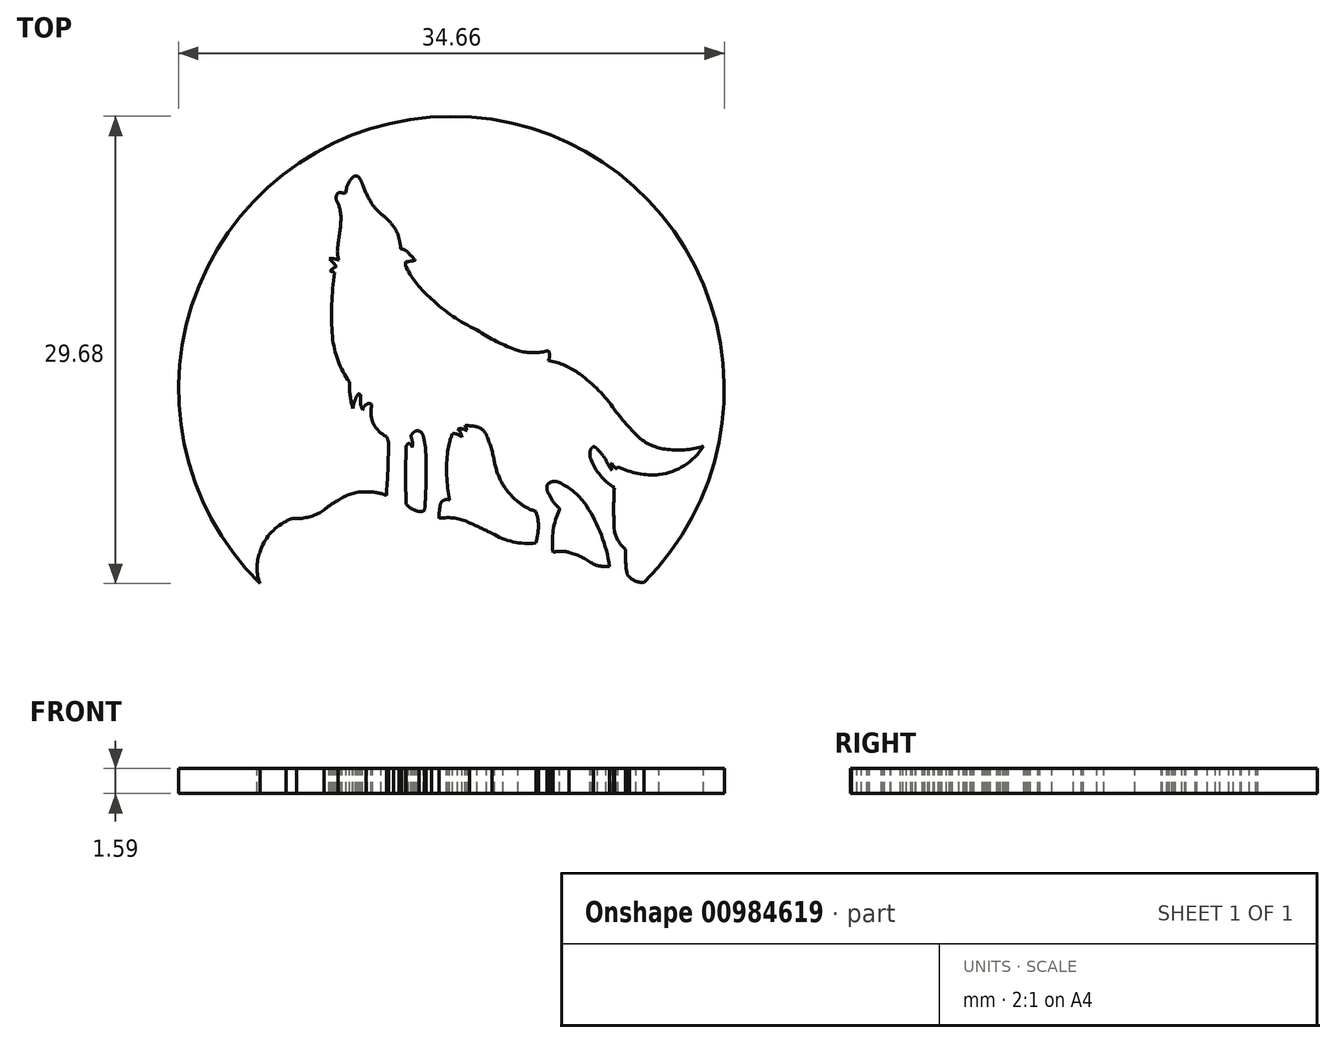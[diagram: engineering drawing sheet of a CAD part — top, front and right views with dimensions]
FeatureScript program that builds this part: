
annotation { "Feature Type Name" : "Feature", "Feature Type Description" : "" }
export const myFeature = defineFeature(function(context is Context, id is Id, definition is map)
    precondition{}
    {
        {
            var Q0;
            Q0=qCreatedBy(makeId("Top.planeOp"),FACE);
            var sketch = newSketch(context, id + "F0", { "sketchPlane" : qUnion([Q0])});
            skArc(sketch, "E0", {"start": v(-39.5, 29.75) * mm, "mid": v(-43.8, 31) * mm, "end": v(-48.06, 29.62) * mm});
            skText(sketch, "E1", { "text": "X", "fontName": "OpenSans-Bold.ttf"});
            skLineSegment(sketch, "E2", {"start": v(-39.5, 28.5) * mm, "end": v(-39.5, 29.75) * mm});
            skLineSegment(sketch, "E3", {"start": v(-39.5, 29.75) * mm, "end": v(-39.5, 28.5) * mm});
            skArc(sketch, "E4.0", {"start": v(-39.5, 28.5) * mm, "mid": v(-43.8, 29.98) * mm, "end": v(-48.06, 28.34) * mm});
            skLineSegment(sketch, "E5", {"start": v(-48.06, 29.62) * mm, "end": v(-48.06, 28.34) * mm});
            skText(sketch, "E6", { "text": "O", "fontName": "OpenSans-Bold.ttf"});
            skArc(sketch, "E7", {"start": v(-29.74, 33.36) * mm, "mid": v(-29.91, 33.5) * mm, "end": v(-30.13, 33.56) * mm});
            skArc(sketch, "E8", {"start": v(-29.44, 32.82) * mm, "mid": v(-29.55, 33.11) * mm, "end": v(-29.74, 33.36) * mm});
            skArc(sketch, "E9", {"start": v(-29.37, 32.03) * mm, "mid": v(-29.37, 32.43) * mm, "end": v(-29.44, 32.82) * mm});
            skArc(sketch, "E10", {"start": v(-29.44, 31.32) * mm, "mid": v(-29.38, 31.68) * mm, "end": v(-29.37, 32.03) * mm});
            skArc(sketch, "E11", {"start": v(-29.97, 30.97) * mm, "mid": v(-29.67, 31.08) * mm, "end": v(-29.44, 31.32) * mm});
            skArc(sketch, "E12", {"start": v(-30.54, 31.17) * mm, "mid": v(-30.28, 31) * mm, "end": v(-29.97, 30.97) * mm});
            skArc(sketch, "E13", {"start": v(-30.9, 32.19) * mm, "mid": v(-30.81, 31.65) * mm, "end": v(-30.54, 31.17) * mm});
            skArc(sketch, "E14", {"start": v(-30.38, 33.44) * mm, "mid": v(-30.77, 32.87) * mm, "end": v(-30.9, 32.19) * mm});
            skArc(sketch, "E15", {"start": v(-30.13, 33.56) * mm, "mid": v(-30.27, 33.53) * mm, "end": v(-30.38, 33.44) * mm});
            skArc(sketch, "E16", {"start": v(-28.5, 35.6) * mm, "mid": v(-28.63, 35.62) * mm, "end": v(-28.75, 35.6) * mm});
            skArc(sketch, "E17", {"start": v(-28.75, 35.6) * mm, "mid": v(-29.02, 35.47) * mm, "end": v(-29.22, 35.24) * mm});
            skArc(sketch, "E18", {"start": v(-29.22, 35.24) * mm, "mid": v(-29.5, 34.6) * mm, "end": v(-29.58, 33.92) * mm});
            skArc(sketch, "E19", {"start": v(-29.58, 33.92) * mm, "mid": v(-29.54, 33.44) * mm, "end": v(-29.37, 32.99) * mm});
            skArc(sketch, "E20", {"start": v(-29.37, 32.99) * mm, "mid": v(-29.1, 32.69) * mm, "end": v(-28.7, 32.55) * mm});
            skArc(sketch, "E21", {"start": v(-28.7, 32.55) * mm, "mid": v(-28.5, 32.57) * mm, "end": v(-28.3, 32.65) * mm});
            skArc(sketch, "E22", {"start": v(-28.3, 32.65) * mm, "mid": v(-28.11, 32.92) * mm, "end": v(-28, 33.23) * mm});
            skArc(sketch, "E23", {"start": v(-28, 33.23) * mm, "mid": v(-27.97, 33.7) * mm, "end": v(-28, 34.16) * mm});
            skArc(sketch, "E24", {"start": v(-28, 34.16) * mm, "mid": v(-28.1, 34.8) * mm, "end": v(-28.34, 35.42) * mm});
            skArc(sketch, "E25", {"start": v(-28.34, 35.42) * mm, "mid": v(-28.4, 35.53) * mm, "end": v(-28.5, 35.6) * mm});
            skArc(sketch, "E26", {"start": v(-30.01, 34.79) * mm, "mid": v(-30.34, 34.33) * mm, "end": v(-30.42, 33.78) * mm});
            skArc(sketch, "E27", {"start": v(-29.95, 34.5) * mm, "mid": v(-29.97, 34.24) * mm, "end": v(-29.93, 33.98) * mm});
            skArc(sketch, "E28", {"start": v(-29.87, 33.78) * mm, "mid": v(-29.9, 33.88) * mm, "end": v(-29.93, 33.98) * mm});
            skArc(sketch, "E29", {"start": v(-29.9, 33.77) * mm, "mid": v(-29.88, 33.8) * mm, "end": v(-29.88, 33.82) * mm});
            skArc(sketch, "E30", {"start": v(-29.94, 33.77) * mm, "mid": v(-29.92, 33.76) * mm, "end": v(-29.9, 33.77) * mm});
            skArc(sketch, "E31", {"start": v(-29.94, 33.77) * mm, "mid": v(-30.12, 33.8) * mm, "end": v(-30.3, 33.77) * mm});
            skArc(sketch, "E32", {"start": v(-30.3, 33.77) * mm, "mid": v(-30.33, 33.75) * mm, "end": v(-30.38, 33.72) * mm});
            skArc(sketch, "E33", {"start": v(-30.42, 33.78) * mm, "mid": v(-30.42, 33.75) * mm, "end": v(-30.41, 33.73) * mm});
            skArc(sketch, "E34", {"start": v(-30.41, 33.73) * mm, "mid": v(-30.4, 33.72) * mm, "end": v(-30.38, 33.72) * mm});
            skArc(sketch, "E35", {"start": v(-29.96, 34.8) * mm, "mid": v(-29.99, 34.8) * mm, "end": v(-30.01, 34.79) * mm});
            skArc(sketch, "E36", {"start": v(-29.94, 34.77) * mm, "mid": v(-29.94, 34.79) * mm, "end": v(-29.96, 34.8) * mm});
            skArc(sketch, "E37", {"start": v(-29.94, 34.66) * mm, "mid": v(-29.94, 34.71) * mm, "end": v(-29.94, 34.77) * mm});
            skPoint(sketch, "E37.startSnap0", {"position": v(-29.94, 34.79) * mm});
            skArc(sketch, "E38", {"start": v(-29.94, 34.66) * mm, "mid": v(-29.95, 34.58) * mm, "end": v(-29.95, 34.5) * mm});
            skLineSegment(sketch, "E39", {"start": v(-27.83, 33.8) * mm, "end": v(-27.83, 34.22) * mm});
            skArc(sketch, "E40.MirrorCS", {"start": v(-25.71, 34.66) * mm, "mid": v(-25.72, 34.71) * mm, "end": v(-25.72, 34.77) * mm});
            skArc(sketch, "E41.MirrorCS", {"start": v(-25.7, 34.8) * mm, "mid": v(-25.66, 34.8) * mm, "end": v(-25.64, 34.79) * mm});
            skArc(sketch, "E42.MirrorCS", {"start": v(-25.72, 34.77) * mm, "mid": v(-25.71, 34.79) * mm, "end": v(-25.7, 34.8) * mm});
            skArc(sketch, "E43.MirrorCS", {"start": v(-25.36, 33.77) * mm, "mid": v(-25.32, 33.75) * mm, "end": v(-25.28, 33.72) * mm});
            skArc(sketch, "E44.MirrorCS", {"start": v(-25.24, 33.73) * mm, "mid": v(-25.26, 33.72) * mm, "end": v(-25.28, 33.72) * mm});
            skArc(sketch, "E45.MirrorCS", {"start": v(-25.23, 33.78) * mm, "mid": v(-25.23, 33.75) * mm, "end": v(-25.24, 33.73) * mm});
            skArc(sketch, "E46.MirrorCS", {"start": v(-25.7, 33.77) * mm, "mid": v(-25.73, 33.76) * mm, "end": v(-25.76, 33.77) * mm});
            skArc(sketch, "E47.MirrorCS", {"start": v(-25.76, 33.77) * mm, "mid": v(-25.77, 33.8) * mm, "end": v(-25.77, 33.82) * mm});
            skArc(sketch, "E48.MirrorCS", {"start": v(-27.14, 35.6) * mm, "mid": v(-27.02, 35.62) * mm, "end": v(-26.9, 35.6) * mm});
            skArc(sketch, "E49.MirrorCS", {"start": v(-25.79, 33.78) * mm, "mid": v(-25.75, 33.88) * mm, "end": v(-25.72, 33.98) * mm});
            skArc(sketch, "E50.MirrorCS", {"start": v(-25.53, 33.56) * mm, "mid": v(-25.38, 33.53) * mm, "end": v(-25.27, 33.44) * mm});
            skArc(sketch, "E51.MirrorCS", {"start": v(-27.32, 35.42) * mm, "mid": v(-27.25, 35.53) * mm, "end": v(-27.14, 35.6) * mm});
            skArc(sketch, "E52.MirrorCS", {"start": v(-25.71, 34.66) * mm, "mid": v(-25.7, 34.58) * mm, "end": v(-25.7, 34.5) * mm});
            skArc(sketch, "E53.MirrorCS", {"start": v(-25.7, 33.77) * mm, "mid": v(-25.53, 33.8) * mm, "end": v(-25.36, 33.77) * mm});
            skArc(sketch, "E54.MirrorCS", {"start": v(-26.9, 35.6) * mm, "mid": v(-26.63, 35.47) * mm, "end": v(-26.43, 35.24) * mm});
            skArc(sketch, "E55.MirrorCS", {"start": v(-25.11, 31.17) * mm, "mid": v(-25.37, 31) * mm, "end": v(-25.68, 30.97) * mm});
            skArc(sketch, "E56.MirrorCS", {"start": v(-26.21, 32.82) * mm, "mid": v(-26.1, 33.11) * mm, "end": v(-25.9, 33.36) * mm});
            skPoint(sketch, "E57.MirrorP", {"position": v(-25.71, 34.79) * mm});
            skArc(sketch, "E58.MirrorCS", {"start": v(-27.65, 33.23) * mm, "mid": v(-27.68, 33.7) * mm, "end": v(-27.65, 34.16) * mm});
            skArc(sketch, "E59.MirrorCS", {"start": v(-27.65, 34.16) * mm, "mid": v(-27.54, 34.8) * mm, "end": v(-27.32, 35.42) * mm});
            skArc(sketch, "E60.MirrorCS", {"start": v(-25.9, 33.36) * mm, "mid": v(-25.74, 33.5) * mm, "end": v(-25.53, 33.56) * mm});
            skArc(sketch, "E61.MirrorCS", {"start": v(-26.94, 32.55) * mm, "mid": v(-27.15, 32.57) * mm, "end": v(-27.35, 32.65) * mm});
            skArc(sketch, "E62.MirrorCS", {"start": v(-25.68, 30.97) * mm, "mid": v(-25.99, 31.08) * mm, "end": v(-26.21, 31.32) * mm});
            skArc(sketch, "E63.MirrorCS", {"start": v(-26.07, 33.92) * mm, "mid": v(-26.12, 33.44) * mm, "end": v(-26.28, 32.99) * mm});
            skArc(sketch, "E64.MirrorCS", {"start": v(-26.28, 32.99) * mm, "mid": v(-26.56, 32.69) * mm, "end": v(-26.94, 32.55) * mm});
            skArc(sketch, "E65.MirrorCS", {"start": v(-25.64, 34.79) * mm, "mid": v(-25.31, 34.33) * mm, "end": v(-25.23, 33.78) * mm});
            skArc(sketch, "E66.MirrorCS", {"start": v(-24.75, 32.19) * mm, "mid": v(-24.84, 31.65) * mm, "end": v(-25.11, 31.17) * mm});
            skArc(sketch, "E67.MirrorCS", {"start": v(-26.21, 31.32) * mm, "mid": v(-26.27, 31.68) * mm, "end": v(-26.29, 32.03) * mm});
            skArc(sketch, "E68.MirrorCS", {"start": v(-26.29, 32.03) * mm, "mid": v(-26.28, 32.43) * mm, "end": v(-26.21, 32.82) * mm});
            skArc(sketch, "E69.MirrorCS", {"start": v(-26.43, 35.24) * mm, "mid": v(-26.15, 34.6) * mm, "end": v(-26.07, 33.92) * mm});
            skArc(sketch, "E70.MirrorCS", {"start": v(-25.27, 33.44) * mm, "mid": v(-24.88, 32.87) * mm, "end": v(-24.75, 32.19) * mm});
            skArc(sketch, "E71.MirrorCS", {"start": v(-27.35, 32.65) * mm, "mid": v(-27.54, 32.92) * mm, "end": v(-27.65, 33.23) * mm});
            skArc(sketch, "E72.MirrorCS", {"start": v(-25.7, 34.5) * mm, "mid": v(-25.69, 34.24) * mm, "end": v(-25.72, 33.98) * mm});
            skArc(sketch, "E73", {"start": v(-28.52, 36.45) * mm, "mid": v(-28.53, 36.36) * mm, "end": v(-28.52, 36.26) * mm});
            skArc(sketch, "E74", {"start": v(-28.55, 36.92) * mm, "mid": v(-28.78, 36.7) * mm, "end": v(-28.9, 36.39) * mm});
            skArc(sketch, "E75", {"start": v(-28.9, 36.39) * mm, "mid": v(-28.97, 36.14) * mm, "end": v(-29, 35.88) * mm});
            skArc(sketch, "E76", {"start": v(-29, 35.88) * mm, "mid": v(-28.98, 35.85) * mm, "end": v(-28.94, 35.86) * mm});
            skArc(sketch, "E77", {"start": v(-28.5, 35.9) * mm, "mid": v(-28.73, 35.92) * mm, "end": v(-28.94, 35.86) * mm});
            skArc(sketch, "E78", {"start": v(-28.5, 35.9) * mm, "mid": v(-28.47, 35.9) * mm, "end": v(-28.46, 35.93) * mm});
            skArc(sketch, "E79", {"start": v(-28.52, 36.26) * mm, "mid": v(-28.5, 36.1) * mm, "end": v(-28.46, 35.93) * mm});
            skPoint(sketch, "E80.start.orphan", {"position": v(-28.48, 36.73) * mm});
            skArc(sketch, "E81", {"start": v(-28.49, 36.87) * mm, "mid": v(-28.51, 36.66) * mm, "end": v(-28.52, 36.45) * mm});
            skArc(sketch, "E82", {"start": v(-28.49, 36.87) * mm, "mid": v(-28.49, 36.89) * mm, "end": v(-28.49, 36.9) * mm});
            skArc(sketch, "E83", {"start": v(-28.5, 36.93) * mm, "mid": v(-28.53, 36.93) * mm, "end": v(-28.55, 36.92) * mm});
            skArc(sketch, "E84", {"start": v(-28.49, 36.9) * mm, "mid": v(-28.5, 36.92) * mm, "end": v(-28.5, 36.93) * mm});
            skPoint(sketch, "E85.start.orphan", {"position": v(-28.48, 36.87) * mm});
            skArc(sketch, "E86.MirrorCS", {"start": v(-27.16, 36.87) * mm, "mid": v(-27.16, 36.89) * mm, "end": v(-27.16, 36.9) * mm});
            skArc(sketch, "E87.MirrorCS", {"start": v(-26.66, 35.88) * mm, "mid": v(-26.68, 35.85) * mm, "end": v(-26.7, 35.86) * mm});
            skArc(sketch, "E88.MirrorCS", {"start": v(-27.16, 36.9) * mm, "mid": v(-27.16, 36.92) * mm, "end": v(-27.15, 36.93) * mm});
            skArc(sketch, "E89.MirrorCS", {"start": v(-27.15, 35.9) * mm, "mid": v(-27.18, 35.9) * mm, "end": v(-27.2, 35.93) * mm});
            skArc(sketch, "E90.MirrorCS", {"start": v(-27.15, 36.93) * mm, "mid": v(-27.13, 36.93) * mm, "end": v(-27.1, 36.92) * mm});
            skArc(sketch, "E91.MirrorCS", {"start": v(-27.1, 36.92) * mm, "mid": v(-26.88, 36.7) * mm, "end": v(-26.75, 36.39) * mm});
            skPoint(sketch, "E92.MirrorP", {"position": v(-27.18, 36.87) * mm});
            skPoint(sketch, "E93.MirrorP", {"position": v(-27.18, 36.73) * mm});
            skArc(sketch, "E94.MirrorCS", {"start": v(-27.13, 36.45) * mm, "mid": v(-27.12, 36.36) * mm, "end": v(-27.13, 36.26) * mm});
            skArc(sketch, "E95.MirrorCS", {"start": v(-27.13, 36.26) * mm, "mid": v(-27.15, 36.1) * mm, "end": v(-27.2, 35.93) * mm});
            skArc(sketch, "E96.MirrorCS", {"start": v(-27.16, 36.87) * mm, "mid": v(-27.14, 36.66) * mm, "end": v(-27.13, 36.45) * mm});
            skArc(sketch, "E97.MirrorCS", {"start": v(-26.75, 36.39) * mm, "mid": v(-26.69, 36.14) * mm, "end": v(-26.66, 35.88) * mm});
            skArc(sketch, "E98.MirrorCS", {"start": v(-27.15, 35.9) * mm, "mid": v(-26.92, 35.92) * mm, "end": v(-26.7, 35.86) * mm});
            skArc(sketch, "E99", {"start": v(-30.1, 29.79) * mm, "mid": v(-29.85, 29.24) * mm, "end": v(-29.3, 29.04) * mm});
            skArc(sketch, "E100", {"start": v(-29.63, 30.73) * mm, "mid": v(-29.95, 30.3) * mm, "end": v(-30.1, 29.79) * mm});
            skArc(sketch, "E101", {"start": v(-29.14, 31.1) * mm, "mid": v(-28.75, 31.41) * mm, "end": v(-28.4, 31.78) * mm});
            skArc(sketch, "E102", {"start": v(-29.14, 31.1) * mm, "mid": v(-29.4, 30.93) * mm, "end": v(-29.63, 30.73) * mm});
            skArc(sketch, "E103", {"start": v(-27.86, 32.17) * mm, "mid": v(-28.18, 32.03) * mm, "end": v(-28.4, 31.78) * mm});
            skArc(sketch, "E104", {"start": v(-27.3, 31.9) * mm, "mid": v(-27.55, 32.1) * mm, "end": v(-27.86, 32.17) * mm});
            skArc(sketch, "E105", {"start": v(-27.02, 31.55) * mm, "mid": v(-27.15, 31.73) * mm, "end": v(-27.3, 31.9) * mm});
            skArc(sketch, "E106", {"start": v(-27.02, 31.55) * mm, "mid": v(-26.77, 31.34) * mm, "end": v(-26.5, 31.15) * mm});
            skArc(sketch, "E107", {"start": v(-25.86, 30.62) * mm, "mid": v(-26.17, 30.9) * mm, "end": v(-26.5, 31.15) * mm});
            skArc(sketch, "E108", {"start": v(-25.51, 29.74) * mm, "mid": v(-25.6, 30.21) * mm, "end": v(-25.86, 30.62) * mm});
            skArc(sketch, "E109", {"start": v(-25.83, 29.19) * mm, "mid": v(-25.61, 29.43) * mm, "end": v(-25.51, 29.74) * mm});
            skArc(sketch, "E110", {"start": v(-26.46, 29.05) * mm, "mid": v(-26.14, 29.06) * mm, "end": v(-25.83, 29.19) * mm});
            skArc(sketch, "E111", {"start": v(-26.7, 29.13) * mm, "mid": v(-26.59, 29.08) * mm, "end": v(-26.46, 29.05) * mm});
            skArc(sketch, "E112", {"start": v(-26.7, 29.13) * mm, "mid": v(-27.24, 29.31) * mm, "end": v(-27.8, 29.38) * mm});
            skArc(sketch, "E113", {"start": v(-27.8, 29.38) * mm, "mid": v(-28.2, 29.33) * mm, "end": v(-28.6, 29.23) * mm});
            skArc(sketch, "E114", {"start": v(-28.6, 29.23) * mm, "mid": v(-28.85, 29.16) * mm, "end": v(-29.1, 29.07) * mm});
            skArc(sketch, "E115", {"start": v(-29.3, 29.04) * mm, "mid": v(-29.2, 29.05) * mm, "end": v(-29.1, 29.07) * mm});
            skCircle(sketch, "E116", {"center": v(28.39, 23.47) * mm, "radius": 17.33 * mm});
            skArc(sketch, "E117", {"start": v(24.26, 16.72) * mm, "mid": v(23.62, 16.9) * mm, "end": v(22.95, 16.95) * mm});
            skArc(sketch, "E118", {"start": v(22.95, 16.95) * mm, "mid": v(22.02, 16.82) * mm, "end": v(21.19, 16.4) * mm});
            skArc(sketch, "E119", {"start": v(21.19, 16.4) * mm, "mid": v(20.73, 16.13) * mm, "end": v(20.3, 15.8) * mm});
            skArc(sketch, "E120", {"start": v(18.54, 15.26) * mm, "mid": v(19.47, 15.39) * mm, "end": v(20.3, 15.8) * mm});
            skArc(sketch, "E121", {"start": v(18.54, 15.26) * mm, "mid": v(18.2, 15.23) * mm, "end": v(17.88, 15.08) * mm});
            skArc(sketch, "E122", {"start": v(17.88, 15.08) * mm, "mid": v(16.85, 14.26) * mm, "end": v(16.23, 13.1) * mm});
            skArc(sketch, "E123", {"start": v(16.23, 13.1) * mm, "mid": v(16.04, 12.11) * mm, "end": v(16.23, 11.12) * mm});
            skArc(sketch, "E124", {"start": v(25.51, 16.16) * mm, "mid": v(25.89, 15.86) * mm, "end": v(26.34, 15.7) * mm});
            skArc(sketch, "E125", {"start": v(26.34, 15.7) * mm, "mid": v(26.53, 15.7) * mm, "end": v(26.69, 15.8) * mm});
            skArc(sketch, "E126", {"start": v(29.54, 14.98) * mm, "mid": v(28.6, 15.28) * mm, "end": v(27.6, 15.26) * mm});
            skArc(sketch, "E127", {"start": v(30.96, 14.32) * mm, "mid": v(30.25, 14.65) * mm, "end": v(29.54, 14.98) * mm});
            skArc(sketch, "E128", {"start": v(30.96, 14.32) * mm, "mid": v(32.3, 13.78) * mm, "end": v(33.75, 13.69) * mm});
            skArc(sketch, "E129", {"start": v(35.84, 13.1) * mm, "mid": v(35.34, 13.17) * mm, "end": v(34.84, 13.1) * mm});
            skArc(sketch, "E130", {"start": v(37.4, 12.35) * mm, "mid": v(36.66, 12.8) * mm, "end": v(35.84, 13.1) * mm});
            skArc(sketch, "E131", {"start": v(37.4, 12.35) * mm, "mid": v(37.92, 12.21) * mm, "end": v(38.44, 12.2) * mm});
            skArc(sketch, "E132", {"start": v(39.7, 11.55) * mm, "mid": v(40.11, 11.26) * mm, "end": v(40.61, 11.19) * mm});
            skArc(sketch, "E133", {"start": v(23.33, 22.37) * mm, "mid": v(23.45, 21.25) * mm, "end": v(24.26, 20.46) * mm});
            skArc(sketch, "E134", {"start": v(23.33, 22.37) * mm, "mid": v(23.25, 22.55) * mm, "end": v(23.05, 22.53) * mm});
            skArc(sketch, "E135", {"start": v(23.05, 22.53) * mm, "mid": v(22.85, 22.37) * mm, "end": v(22.76, 22.14) * mm});
            skArc(sketch, "E136", {"start": v(22.62, 22.51) * mm, "mid": v(22.67, 22.32) * mm, "end": v(22.76, 22.14) * mm});
            skArc(sketch, "E137", {"start": v(22.62, 23.05) * mm, "mid": v(22.54, 23.15) * mm, "end": v(22.42, 23.1) * mm});
            skArc(sketch, "E138", {"start": v(22.62, 23.05) * mm, "mid": v(22.6, 22.78) * mm, "end": v(22.62, 22.51) * mm});
            skArc(sketch, "E139", {"start": v(22.42, 23.1) * mm, "mid": v(22.23, 22.68) * mm, "end": v(22.12, 22.24) * mm});
            skArc(sketch, "E140", {"start": v(21.9, 23.91) * mm, "mid": v(21.96, 23.07) * mm, "end": v(22.12, 22.24) * mm});
            skArc(sketch, "E141", {"start": v(24.4, 19.91) * mm, "mid": v(24.36, 20.2) * mm, "end": v(24.26, 20.46) * mm});
            skArc(sketch, "E142", {"start": v(24.26, 16.72) * mm, "mid": v(24.35, 18.32) * mm, "end": v(24.4, 19.91) * mm});
            skArc(sketch, "E143", {"start": v(25.51, 19.77) * mm, "mid": v(25.48, 17.96) * mm, "end": v(25.51, 16.16) * mm});
            skArc(sketch, "E144", {"start": v(25.65, 20.02) * mm, "mid": v(25.55, 19.91) * mm, "end": v(25.51, 19.77) * mm});
            skArc(sketch, "E145", {"start": v(25.9, 19.77) * mm, "mid": v(25.82, 19.94) * mm, "end": v(25.65, 20.02) * mm});
            skArc(sketch, "E146", {"start": v(25.9, 19.77) * mm, "mid": v(25.91, 20.1) * mm, "end": v(25.83, 20.43) * mm});
            skArc(sketch, "E147", {"start": v(25.9, 20.64) * mm, "mid": v(25.83, 20.54) * mm, "end": v(25.83, 20.43) * mm});
            skArc(sketch, "E148", {"start": v(26.2, 20.83) * mm, "mid": v(26.03, 20.76) * mm, "end": v(25.9, 20.64) * mm});
            skArc(sketch, "E149", {"start": v(26.6, 20.43) * mm, "mid": v(26.48, 20.7) * mm, "end": v(26.2, 20.83) * mm});
            skArc(sketch, "E150", {"start": v(26.76, 19.5) * mm, "mid": v(26.7, 19.97) * mm, "end": v(26.6, 20.43) * mm});
            skArc(sketch, "E151", {"start": v(26.69, 15.8) * mm, "mid": v(26.78, 17.66) * mm, "end": v(26.76, 19.5) * mm});
            skArc(sketch, "E152", {"start": v(20.83, 26.8) * mm, "mid": v(21.18, 25.29) * mm, "end": v(21.9, 23.91) * mm});
            skArc(sketch, "E153", {"start": v(20.96, 30.86) * mm, "mid": v(20.79, 28.83) * mm, "end": v(20.83, 26.8) * mm});
            skArc(sketch, "E154", {"start": v(20.96, 30.86) * mm, "mid": v(20.83, 30.93) * mm, "end": v(20.68, 30.96) * mm});
            skArc(sketch, "E155", {"start": v(21.07, 31.25) * mm, "mid": v(20.86, 31.13) * mm, "end": v(20.68, 30.96) * mm});
            skArc(sketch, "E156", {"start": v(21.07, 31.25) * mm, "mid": v(20.87, 31.53) * mm, "end": v(20.6, 31.75) * mm});
            skArc(sketch, "E157", {"start": v(21.25, 31.66) * mm, "mid": v(20.94, 31.75) * mm, "end": v(20.6, 31.75) * mm});
            skArc(sketch, "E158", {"start": v(21.16, 32.44) * mm, "mid": v(21.15, 32.05) * mm, "end": v(21.25, 31.66) * mm});
            skArc(sketch, "E159", {"start": v(21.25, 33.14) * mm, "mid": v(21.2, 32.79) * mm, "end": v(21.16, 32.44) * mm});
            skArc(sketch, "E160", {"start": v(21.25, 33.14) * mm, "mid": v(21.33, 33.73) * mm, "end": v(21.37, 34.32) * mm});
            skArc(sketch, "E161", {"start": v(21.37, 34.32) * mm, "mid": v(21.3, 34.9) * mm, "end": v(21.1, 35.46) * mm});
            skArc(sketch, "E162", {"start": v(21.16, 35.9) * mm, "mid": v(21.06, 35.69) * mm, "end": v(21.1, 35.46) * mm});
            skArc(sketch, "E163", {"start": v(21.46, 35.94) * mm, "mid": v(21.3, 35.96) * mm, "end": v(21.16, 35.9) * mm});
            skArc(sketch, "E164", {"start": v(21.46, 35.94) * mm, "mid": v(21.58, 35.92) * mm, "end": v(21.7, 35.96) * mm});
            skArc(sketch, "E165", {"start": v(22.13, 36.94) * mm, "mid": v(21.81, 36.5) * mm, "end": v(21.7, 35.96) * mm});
            skArc(sketch, "E166", {"start": v(22.3, 37.01) * mm, "mid": v(22.2, 37) * mm, "end": v(22.13, 36.94) * mm});
            skArc(sketch, "E167", {"start": v(22.53, 36.9) * mm, "mid": v(22.43, 37) * mm, "end": v(22.3, 37.01) * mm});
            skArc(sketch, "E168", {"start": v(22.74, 36.47) * mm, "mid": v(22.65, 36.7) * mm, "end": v(22.53, 36.9) * mm});
            skArc(sketch, "E169", {"start": v(22.74, 36.47) * mm, "mid": v(23.02, 35.8) * mm, "end": v(23.38, 35.17) * mm});
            skArc(sketch, "E170", {"start": v(23.38, 35.17) * mm, "mid": v(23.63, 34.88) * mm, "end": v(23.9, 34.6) * mm});
            skArc(sketch, "E171", {"start": v(24.7, 33.8) * mm, "mid": v(24.34, 34.24) * mm, "end": v(23.9, 34.6) * mm});
            skArc(sketch, "E172", {"start": v(25.05, 33.04) * mm, "mid": v(24.93, 33.44) * mm, "end": v(24.7, 33.8) * mm});
            skArc(sketch, "E173", {"start": v(25.16, 32.42) * mm, "mid": v(25.12, 32.73) * mm, "end": v(25.05, 33.04) * mm});
            skArc(sketch, "E174", {"start": v(25.16, 32.42) * mm, "mid": v(25.18, 32.39) * mm, "end": v(25.22, 32.36) * mm});
            skArc(sketch, "E175", {"start": v(25.6, 32.18) * mm, "mid": v(25.43, 32.31) * mm, "end": v(25.22, 32.36) * mm});
            skArc(sketch, "E176", {"start": v(25.6, 32.18) * mm, "mid": v(25.82, 31.94) * mm, "end": v(26.05, 31.72) * mm});
            skArc(sketch, "E177", {"start": v(26.03, 31.63) * mm, "mid": v(25.85, 31.61) * mm, "end": v(25.68, 31.57) * mm});
            skArc(sketch, "E178", {"start": v(25.51, 31.57) * mm, "mid": v(25.6, 31.56) * mm, "end": v(25.68, 31.57) * mm});
            skArc(sketch, "E179", {"start": v(25.51, 31.57) * mm, "mid": v(25.47, 31.48) * mm, "end": v(25.47, 31.38) * mm});
            skArc(sketch, "E180", {"start": v(25.47, 31.38) * mm, "mid": v(25.48, 31.3) * mm, "end": v(25.51, 31.22) * mm});
            skArc(sketch, "E181.trimOffspring", {"start": v(26.03, 31.63) * mm, "mid": v(26.07, 31.66) * mm, "end": v(26.05, 31.72) * mm});
            skArc(sketch, "E182", {"start": v(25.51, 31.22) * mm, "mid": v(26.2, 30.13) * mm, "end": v(27.11, 29.2) * mm});
            skArc(sketch, "E183", {"start": v(27.11, 29.2) * mm, "mid": v(28.48, 28.1) * mm, "end": v(30, 27.24) * mm});
            skArc(sketch, "E184", {"start": v(30, 27.24) * mm, "mid": v(31.27, 26.5) * mm, "end": v(32.6, 25.92) * mm});
            skArc(sketch, "E185", {"start": v(32.6, 25.92) * mm, "mid": v(33.58, 25.79) * mm, "end": v(34.55, 25.92) * mm});
            skArc(sketch, "E186", {"start": v(34.55, 25.3) * mm, "mid": v(34.62, 25.6) * mm, "end": v(34.55, 25.92) * mm});
            skArc(sketch, "E187", {"start": v(36.54, 24.42) * mm, "mid": v(35.6, 24.97) * mm, "end": v(34.55, 25.3) * mm});
            skArc(sketch, "E188", {"start": v(38.74, 22.16) * mm, "mid": v(37.74, 23.39) * mm, "end": v(36.54, 24.42) * mm});
            skArc(sketch, "E189", {"start": v(38.74, 22.16) * mm, "mid": v(39.4, 21.35) * mm, "end": v(40.1, 20.57) * mm});
            skArc(sketch, "E190", {"start": v(40.1, 20.57) * mm, "mid": v(40.95, 19.97) * mm, "end": v(41.95, 19.66) * mm});
            skArc(sketch, "E191", {"start": v(41.95, 19.66) * mm, "mid": v(43.19, 19.62) * mm, "end": v(44.4, 19.85) * mm});
            skArc(sketch, "E192", {"start": v(41.58, 18.04) * mm, "mid": v(43.2, 18.62) * mm, "end": v(44.4, 19.85) * mm});
            skArc(sketch, "E193", {"start": v(38.98, 18.53) * mm, "mid": v(40.24, 18.1) * mm, "end": v(41.58, 18.04) * mm});
            skArc(sketch, "E194", {"start": v(38.98, 18.53) * mm, "mid": v(38.92, 18.47) * mm, "end": v(38.88, 18.4) * mm});
            skArc(sketch, "E195", {"start": v(38.58, 18.76) * mm, "mid": v(38.7, 18.56) * mm, "end": v(38.88, 18.4) * mm});
            skArc(sketch, "E196", {"start": v(38.58, 18.76) * mm, "mid": v(38.55, 18.54) * mm, "end": v(38.58, 18.3) * mm});
            skArc(sketch, "E197", {"start": v(38.22, 18.92) * mm, "mid": v(38.38, 18.6) * mm, "end": v(38.58, 18.3) * mm});
            skArc(sketch, "E198", {"start": v(38.22, 18.92) * mm, "mid": v(37.96, 19.3) * mm, "end": v(37.66, 19.66) * mm});
            skArc(sketch, "E199", {"start": v(37.66, 19.66) * mm, "mid": v(37.55, 19.76) * mm, "end": v(37.41, 19.82) * mm});
            skArc(sketch, "E200", {"start": v(37.41, 19.82) * mm, "mid": v(37.29, 19.72) * mm, "end": v(37.2, 19.58) * mm});
            skArc(sketch, "E201", {"start": v(37.2, 19.58) * mm, "mid": v(37.18, 19.28) * mm, "end": v(37.25, 19) * mm});
            skArc(sketch, "E202", {"start": v(37.25, 19) * mm, "mid": v(37.84, 17.98) * mm, "end": v(38.73, 17.22) * mm});
            skArc(sketch, "E203", {"start": v(38.73, 17.22) * mm, "mid": v(38.7, 15.85) * mm, "end": v(38.73, 14.48) * mm});
            skArc(sketch, "E204", {"start": v(38.73, 14.48) * mm, "mid": v(39, 13.82) * mm, "end": v(39.44, 13.28) * mm});
            skArc(sketch, "E205", {"start": v(39.44, 13.28) * mm, "mid": v(39.45, 12.55) * mm, "end": v(39.53, 11.82) * mm});
            skArc(sketch, "E206", {"start": v(39.53, 11.82) * mm, "mid": v(39.58, 11.66) * mm, "end": v(39.7, 11.55) * mm});
            skArc(sketch, "E207", {"start": v(35.25, 15.84) * mm, "mid": v(34.85, 14.5) * mm, "end": v(34.84, 13.1) * mm});
            skArc(sketch, "E208", {"start": v(38.44, 12.2) * mm, "mid": v(37.9, 14.2) * mm, "end": v(36.97, 16.05) * mm});
            skArc(sketch, "E209", {"start": v(36.97, 16.05) * mm, "mid": v(36.22, 16.9) * mm, "end": v(35.26, 17.53) * mm});
            skArc(sketch, "E210", {"start": v(35.26, 17.53) * mm, "mid": v(34.85, 17.6) * mm, "end": v(34.48, 17.4) * mm});
            skArc(sketch, "E211", {"start": v(34.48, 17.4) * mm, "mid": v(34.45, 17.1) * mm, "end": v(34.57, 16.82) * mm});
            skArc(sketch, "E212", {"start": v(34.57, 16.82) * mm, "mid": v(34.87, 16.3) * mm, "end": v(35.26, 15.87) * mm});
            skArc(sketch, "E213", {"start": v(35.26, 15.87) * mm, "mid": v(35.26, 15.85) * mm, "end": v(35.25, 15.84) * mm});
            skArc(sketch, "E214", {"start": v(28.28, 16.42) * mm, "mid": v(27.88, 16.4) * mm, "end": v(27.67, 16.05) * mm});
            skArc(sketch, "E215", {"start": v(27.67, 16.05) * mm, "mid": v(27.61, 15.65) * mm, "end": v(27.6, 15.26) * mm});
            skArc(sketch, "E216", {"start": v(28.15, 19.55) * mm, "mid": v(28.1, 17.98) * mm, "end": v(28.28, 16.42) * mm});
            skArc(sketch, "E217", {"start": v(28.46, 20.67) * mm, "mid": v(28.27, 20.12) * mm, "end": v(28.15, 19.55) * mm});
            skArc(sketch, "E218", {"start": v(29.07, 20.42) * mm, "mid": v(28.78, 20.6) * mm, "end": v(28.46, 20.67) * mm});
            skArc(sketch, "E219", {"start": v(29.07, 20.42) * mm, "mid": v(28.96, 20.7) * mm, "end": v(28.78, 20.94) * mm});
            skPoint(sketch, "E219.endSnap0", {"position": v(28.78, 20.6) * mm});
            skArc(sketch, "E220", {"start": v(29.37, 20.83) * mm, "mid": v(29.09, 20.94) * mm, "end": v(28.78, 20.94) * mm});
            skArc(sketch, "E221", {"start": v(29.37, 20.83) * mm, "mid": v(29.32, 21) * mm, "end": v(29.24, 21.15) * mm});
            skArc(sketch, "E222", {"start": v(30, 21.08) * mm, "mid": v(29.63, 21.14) * mm, "end": v(29.24, 21.15) * mm});
            skArc(sketch, "E223", {"start": v(30.63, 20.5) * mm, "mid": v(30.39, 20.87) * mm, "end": v(30, 21.08) * mm});
            skArc(sketch, "E224", {"start": v(31.12, 18.83) * mm, "mid": v(30.93, 19.68) * mm, "end": v(30.63, 20.5) * mm});
            skArc(sketch, "E225", {"start": v(31.12, 18.83) * mm, "mid": v(31.33, 18.1) * mm, "end": v(31.66, 17.4) * mm});
            skArc(sketch, "E226", {"start": v(31.66, 17.4) * mm, "mid": v(32.1, 16.8) * mm, "end": v(32.65, 16.29) * mm});
            skArc(sketch, "E227", {"start": v(32.65, 16.29) * mm, "mid": v(33.17, 15.94) * mm, "end": v(33.75, 15.7) * mm});
            skArc(sketch, "E228", {"start": v(33.91, 14.7) * mm, "mid": v(33.88, 15.2) * mm, "end": v(33.75, 15.7) * mm});
            skArc(sketch, "E229", {"start": v(33.75, 13.69) * mm, "mid": v(33.86, 14.19) * mm, "end": v(33.91, 14.7) * mm});
            skLineSegment(sketch, "E230", {"start": v(-48.81, 37.68) * mm, "end": v(-47.69, 37.68) * mm});
            skLineSegment(sketch, "E231", {"start": v(-48.81, 37.68) * mm, "end": v(-48.81, 32.73) * mm});
            skLineSegment(sketch, "E232", {"start": v(-48.81, 32.73) * mm, "end": v(-44.3, 32.73) * mm});
            skLineSegment(sketch, "E233", {"start": v(-44.3, 32.73) * mm, "end": v(-44.3, 37.68) * mm});
            skLineSegment(sketch, "E234", {"start": v(-46.56, 32.73) * mm, "end": v(-46.56, 37.68) * mm});
            skLineSegment(sketch, "E235", {"start": v(-23.05, 66.48) * mm, "end": v(-25.64, 62.67) * mm});
            skLineSegment(sketch, "E236", {"start": v(-25.7, 66.49) * mm, "end": v(-23.07, 62.65) * mm});
            skPoint(sketch, "E237.orphan", {"position": v(-24.37, 67.03) * mm});
            skPoint(sketch, "E238.orphan", {"position": v(-22.11, 67.03) * mm});
            skPoint(sketch, "E239.start.orphan", {"position": v(-22.11, 64.55) * mm});
            skPoint(sketch, "E240.end.orphan", {"position": v(-24.37, 64.55) * mm});
            skPoint(sketch, "E240.start.orphan", {"position": v(-24.37, 62.07) * mm});
            skPoint(sketch, "E241.MirrorP", {"position": v(-19.86, 64.55) * mm});
            skLineSegment(sketch, "E242.0", {"start": v(-17.6, 66.5) * mm, "end": v(-17.6, 66.5) * mm});
            skArc(sketch, "E243", {"start": v(-18.13, 64.55) * mm, "mid": v(-18.17, 64.9) * mm, "end": v(-18.26, 65.23) * mm});
            skArc(sketch, "E244", {"start": v(-19.12, 66.3) * mm, "mid": v(-19.35, 66.4) * mm, "end": v(-19.6, 66.47) * mm});
            skArc(sketch, "E245", {"start": v(-18.26, 65.23) * mm, "mid": v(-18.58, 65.85) * mm, "end": v(-19.12, 66.3) * mm});
            skArc(sketch, "E246.MirrorCS", {"start": v(-20.6, 66.3) * mm, "mid": v(-20.37, 66.4) * mm, "end": v(-20.12, 66.47) * mm});
            skArc(sketch, "E247.MirrorCS", {"start": v(-21.45, 65.23) * mm, "mid": v(-21.13, 65.85) * mm, "end": v(-20.6, 66.3) * mm});
            skArc(sketch, "E248.MirrorCS", {"start": v(-21.58, 64.55) * mm, "mid": v(-21.54, 64.9) * mm, "end": v(-21.45, 65.23) * mm});
            skArc(sketch, "E249.MirrorCS", {"start": v(-18.13, 64.55) * mm, "mid": v(-18.17, 64.2) * mm, "end": v(-18.26, 63.86) * mm});
            skArc(sketch, "E250.MirrorCS", {"start": v(-18.26, 63.86) * mm, "mid": v(-18.58, 63.24) * mm, "end": v(-19.12, 62.8) * mm});
            skArc(sketch, "E251.MirrorCS", {"start": v(-19.12, 62.8) * mm, "mid": v(-19.35, 62.7) * mm, "end": v(-19.6, 62.62) * mm});
            skArc(sketch, "E252.MirrorCS", {"start": v(-20.6, 62.8) * mm, "mid": v(-20.37, 62.7) * mm, "end": v(-20.12, 62.62) * mm});
            skArc(sketch, "E253.MirrorCS", {"start": v(-21.45, 63.86) * mm, "mid": v(-21.13, 63.24) * mm, "end": v(-20.6, 62.8) * mm});
            skArc(sketch, "E254.MirrorCS", {"start": v(-21.58, 64.55) * mm, "mid": v(-21.54, 64.2) * mm, "end": v(-21.45, 63.86) * mm});
            skPoint(sketch, "E255.orphan", {"position": v(-22.11, 66.5) * mm});
            skPoint(sketch, "E256.orphan", {"position": v(-18.13, 67.03) * mm});
            skPoint(sketch, "E257.start.orphan", {"position": v(-19.86, 67.03) * mm});
            skPoint(sketch, "E258.endSnap0", {"position": v(-20.37, 62.7) * mm});
            skPoint(sketch, "E259.start.orphan", {"position": v(-19.8, 62.07) * mm});
            skPoint(sketch, "E260.start.orphan", {"position": v(-18.13, 62.1) * mm});
            skPoint(sketch, "E261.start.orphan", {"position": v(-25.64, 62.07) * mm});
            skPoint(sketch, "E262.end.orphan", {"position": v(-24.96, 59.87) * mm});
            skPoint(sketch, "E262.start.orphan", {"position": v(-25, 62.07) * mm});
            skPoint(sketch, "E263.end.orphan", {"position": v(-18.97, 59.87) * mm});
            skPoint(sketch, "E263.start.orphan", {"position": v(-18.97, 62.08) * mm});
            skArc(sketch, "E264", {"start": v(-18.97, 59.87) * mm, "mid": v(-21.97, 61.34) * mm, "end": v(-24.96, 59.87) * mm});
            skLineSegment(sketch, "E265", {"start": v(-12.66, 66.48) * mm, "end": v(-15.26, 62.67) * mm});
            skLineSegment(sketch, "E266", {"start": v(-15.3, 66.49) * mm, "end": v(-12.69, 62.65) * mm});
            skPoint(sketch, "E267.orphan", {"position": v(-13.98, 67.03) * mm});
            skPoint(sketch, "E268.orphan", {"position": v(-11.72, 67.03) * mm});
            skPoint(sketch, "E269.start.orphan", {"position": v(-11.72, 64.55) * mm});
            skPoint(sketch, "E270.end.orphan", {"position": v(-13.98, 64.55) * mm});
            skPoint(sketch, "E270.start.orphan", {"position": v(-13.98, 62.07) * mm});
            skPoint(sketch, "E271.MirrorP", {"position": v(-9.47, 64.55) * mm});
            skLineSegment(sketch, "E272.0", {"start": v(-7.2, 66.5) * mm, "end": v(-7.21, 66.5) * mm});
            skArc(sketch, "E273", {"start": v(-7.75, 64.55) * mm, "mid": v(-7.78, 64.9) * mm, "end": v(-7.88, 65.23) * mm});
            skArc(sketch, "E274", {"start": v(-8.73, 66.3) * mm, "mid": v(-8.96, 66.4) * mm, "end": v(-9.2, 66.47) * mm});
            skArc(sketch, "E275", {"start": v(-7.88, 65.23) * mm, "mid": v(-8.2, 65.85) * mm, "end": v(-8.73, 66.3) * mm});
            skArc(sketch, "E276.MirrorCS", {"start": v(-10.2, 66.3) * mm, "mid": v(-9.98, 66.4) * mm, "end": v(-9.73, 66.47) * mm});
            skArc(sketch, "E277.MirrorCS", {"start": v(-11.06, 65.23) * mm, "mid": v(-10.75, 65.85) * mm, "end": v(-10.2, 66.3) * mm});
            skArc(sketch, "E278.MirrorCS", {"start": v(-11.2, 64.55) * mm, "mid": v(-11.16, 64.9) * mm, "end": v(-11.06, 65.23) * mm});
            skArc(sketch, "E279.MirrorCS", {"start": v(-7.75, 64.55) * mm, "mid": v(-7.78, 64.2) * mm, "end": v(-7.88, 63.86) * mm});
            skArc(sketch, "E280.MirrorCS", {"start": v(-7.88, 63.86) * mm, "mid": v(-8.2, 63.24) * mm, "end": v(-8.73, 62.8) * mm});
            skArc(sketch, "E281.MirrorCS", {"start": v(-8.73, 62.8) * mm, "mid": v(-8.96, 62.7) * mm, "end": v(-9.2, 62.62) * mm});
            skArc(sketch, "E282.MirrorCS", {"start": v(-10.2, 62.8) * mm, "mid": v(-9.98, 62.7) * mm, "end": v(-9.73, 62.62) * mm});
            skArc(sketch, "E283.MirrorCS", {"start": v(-11.06, 63.86) * mm, "mid": v(-10.75, 63.24) * mm, "end": v(-10.2, 62.8) * mm});
            skArc(sketch, "E284.MirrorCS", {"start": v(-11.2, 64.55) * mm, "mid": v(-11.16, 64.2) * mm, "end": v(-11.06, 63.86) * mm});
            skPoint(sketch, "E285.orphan", {"position": v(-11.72, 66.5) * mm});
            skPoint(sketch, "E286.orphan", {"position": v(-7.75, 67.03) * mm});
            skPoint(sketch, "E287.start.orphan", {"position": v(-9.47, 67.03) * mm});
            skPoint(sketch, "E288.endSnap0", {"position": v(-9.98, 62.7) * mm});
            skPoint(sketch, "E289.start.orphan", {"position": v(-9.42, 62.07) * mm});
            skPoint(sketch, "E290.start.orphan", {"position": v(-7.75, 62.1) * mm});
            skPoint(sketch, "E291.start.orphan", {"position": v(-15.26, 62.07) * mm});
            skPoint(sketch, "E292.end.orphan", {"position": v(-14.58, 59.87) * mm});
            skPoint(sketch, "E292.start.orphan", {"position": v(-14.62, 62.07) * mm});
            skPoint(sketch, "E293.end.orphan", {"position": v(-8.58, 59.87) * mm});
            skPoint(sketch, "E293.start.orphan", {"position": v(-8.58, 62.08) * mm});
            skArc(sketch, "E294", {"start": v(-8.58, 59.87) * mm, "mid": v(-11.58, 61.34) * mm, "end": v(-14.58, 59.87) * mm});
            skArc(sketch, "E295", {"start": v(-9.2, 66.47) * mm, "mid": v(-9.47, 66.5) * mm, "end": v(-9.73, 66.47) * mm});
            skArc(sketch, "E296.MirrorCS", {"start": v(-9.2, 62.62) * mm, "mid": v(-9.47, 62.6) * mm, "end": v(-9.73, 62.62) * mm});
            const initialGuessF0  = {"E1": [-0.04373, 0.03768, -1, 0, 0.005], "E6": [-0.03816, 0.03768, -1, 0, 0.005]};
            skSetInitialGuess(sketch, initialGuessF0);
            skSolve(sketch);
        }
        {
            var Q0;
            Q0=makeQuery(id+"F0.imprint","IMPRINT",FACE,{"disambiguationData":[TD([[makeQuery(id+"F0.imprint","IMPRINT",EDGE,{"derivedFrom":sQuery(id+"F0.wireOp",EDGE,"E117")}),-1.0]])]});
            var Q1;
            Q1=makeQuery(id+"F0.imprint","IMPRINT",FACE,{"disambiguationData":[TD([[makeQuery(id+"F0.imprint","IMPRINT",EDGE,{"derivedFrom":sQuery(id+"F0.wireOp",EDGE,"E124")}),1.0]])]});
            var Q2;
            Q2=makeQuery(id+"F0.imprint","IMPRINT",FACE,{"disambiguationData":[TD([[makeQuery(id+"F0.imprint","IMPRINT",EDGE,{"derivedFrom":sQuery(id+"F0.wireOp",EDGE,"E126")}),-1.0]])]});
            var Q3;
            Q3=makeQuery(id+"F0.imprint","IMPRINT",FACE,{"disambiguationData":[TD([[makeQuery(id+"F0.imprint","IMPRINT",EDGE,{"derivedFrom":sQuery(id+"F0.wireOp",EDGE,"E129")}),-1.0]])]});
            extrude(context, id + "F1", {"entities" : qUnion([Q0, Q1, Q2, Q3]), "oppositeDirection" : true, "depth" : 1.59 * mm, "offsetDistance" : 25.4 * mm});
        }
    });
